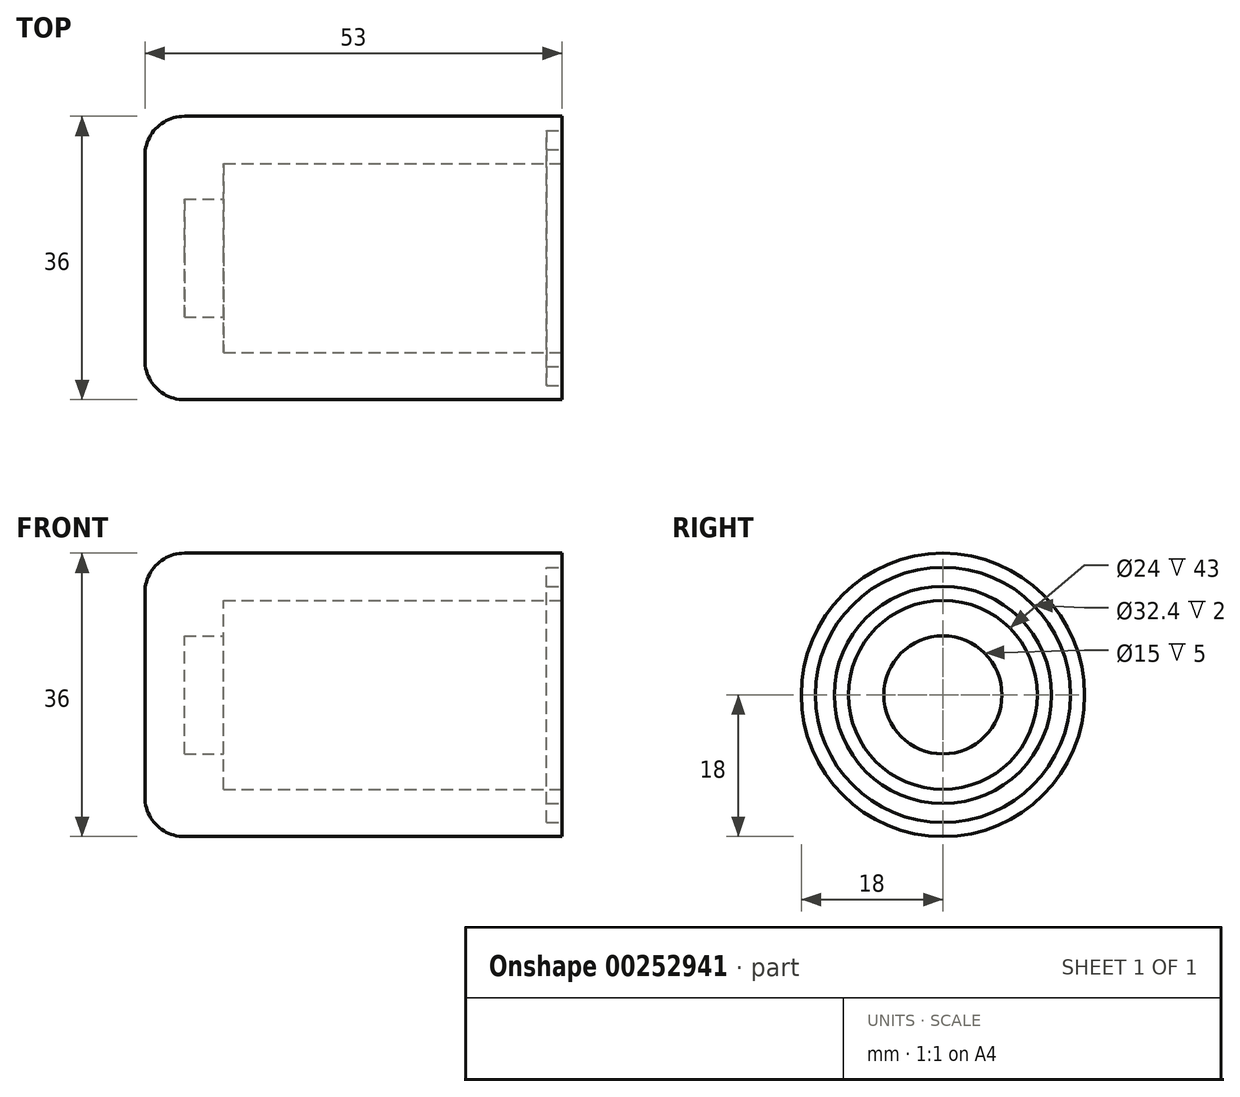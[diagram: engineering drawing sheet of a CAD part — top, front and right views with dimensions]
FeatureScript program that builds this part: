
annotation { "Feature Type Name" : "Feature", "Feature Type Description" : "" }
export const myFeature = defineFeature(function(context is Context, id is Id, definition is map)
    precondition{}
    {
        {
            var Q0;
            Q0=qCreatedBy(makeId("Front.planeOp"),FACE);
            var sketch = newSketch(context, id + "F0", { "sketchPlane" : qUnion([Q0])});
            skLineSegment(sketch, "E0", {"start": v(0, 0) * mm, "end": v(0, 18) * mm});
            skLineSegment(sketch, "E1", {"start": v(0, 18) * mm, "end": v(53, 18) * mm});
            skLineSegment(sketch, "E2", {"start": v(53, 12) * mm, "end": v(10, 12) * mm});
            skLineSegment(sketch, "E3", {"start": v(10, 12) * mm, "end": v(10, 7.5) * mm});
            skLineSegment(sketch, "E4", {"start": v(10, 7.5) * mm, "end": v(5, 7.5) * mm});
            skLineSegment(sketch, "E5", {"start": v(5, 7.5) * mm, "end": v(5, 0) * mm});
            skLineSegment(sketch, "E6", {"start": v(5, 0) * mm, "end": v(0, 0) * mm});
            skLineSegment(sketch, "E7", {"start": v(53, 12) * mm, "end": v(53, 13.8) * mm});
            skLineSegment(sketch, "E8", {"start": v(53, 13.8) * mm, "end": v(51, 13.8) * mm});
            skLineSegment(sketch, "E9", {"start": v(51, 13.8) * mm, "end": v(51, 16.2) * mm});
            skLineSegment(sketch, "E10", {"start": v(51, 16.2) * mm, "end": v(53, 16.2) * mm});
            skLineSegment(sketch, "E11", {"start": v(53, 16.2) * mm, "end": v(53, 18) * mm});
            skPoint(sketch, "E12", {"position": v(51, 15) * mm});
            skSolve(sketch);
        }
        {
            var Q0;
            Q0=makeQuery(id+"F0.imprint","IMPRINT",FACE,{"disambiguationData":[TD([[makeQuery(id+"F0.imprint","IMPRINT",EDGE,{"derivedFrom":sQuery(id+"F0.wireOp",EDGE,"E0")}),-1.0]])]});
            var Q1;
            Q1=sQuery(id+"F0.wireOp",EDGE,"E6");
            revolve(context, id + "F1", {"entities" : qUnion([Q0]), "axis" : qUnion([Q1]), "revolveType" : RevolveType.FULL});
        }
        {
            var Q0;
            Q0=makeQuery(id+"F1.opRevolve","SWEPT_EDGE",EDGE,{"disambiguationData":[OSD([sQuery(id+"F0.wireOp",EDGE,"E0"),sQuery(id+"F0.wireOp",EDGE,"E1")])]});
            fillet(context, id + "F2", {"entities" : qUnion([Q0]), "radius" : 5 * mm, "tangentPropagation" : true, "allowEdgeOverflow" : false});
        }
    });
